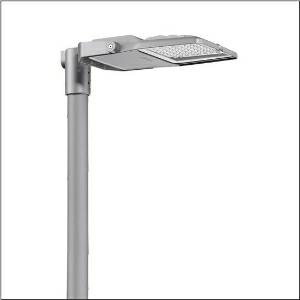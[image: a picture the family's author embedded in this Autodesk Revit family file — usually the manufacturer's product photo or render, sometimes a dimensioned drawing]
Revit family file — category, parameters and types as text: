
# Revit family: floodlight_fl_21_mini___pl61_5xa7771c4c3a_eca3
name_source: partatom
category: Lighting Fixtures
units: mm (PartAtom-declared; Revit-internal decimal feet)

## family parameters
Cut with Voids When Loaded = No
Host = Face
Light Source = No
Part Type = Normal
Room Calculation Point = No
Round Connector Dimension = Use Diameter
Shared = No

## types (1)
- --- (1 x LED, 12490 lm, 87.2 W, 4000K)
    Apparent Load = 87 VA
    CIE Flux Codes = 33 65 98 100 100
    Color Rendering = 70
    Color Temperature = 4000K
    Default Elevation = 1800 mm
    Description = Floodlight FL 21 mini, floodlight, primary light control with lens, of PMMA, primary optical cover: protective disc, of toughened safety glass, transparent, light distribution: PL61, light emission: direct distribution, installation type: surface-mounted, LED, High Power LED, rated luminous flux: 12.490lm, luminous efficacy: 143lm/W, light colour: 740, colour temperature: 4000K, control gear: ECG iQ, control: Auto-Match, Temp-Guard, Lumen-Switch, Night-Set, Smart-Wire, Light-Fading, Desk-Remote (wireless, voltage-free reading and setting of iQ features in the workshop via application-optimized NFC function/RFID function), optimised constant luminous flux control (CLO 2.0), with terminal, 6-pole, mains connection: 220..240V, AC, 50/60Hz, start of lifetime: 87W, end of lifetime: 92W, reduction: 40W, luminaire housing, of diecast aluminium, powder-coated, Siteco® metallic grey (DB 702S), corrosivity category C5 according to DIN EN ISO 12944, mast bracket, of steel, galvanised, powder-coated, Siteco® metallic grey (DB 702S), protection rating (complete): IP66, insulation class (complete): insulation class II (safety insulation), certification: CE, ENEC, VDE, protection symbol: D, impact resistance: IK08, permissible operating ambient temperature: -40..+40°C, permissible operating ambient temperature for outdoor applications: -40..+50°C, standard: DIN EN 12944, packaging unit: 1 piece

Light Distribution: PL61
    Height = 70 mm
    Lamp = 1 x LED
    Lamp Light Flux = 12490 lm
    Lamp Power = 87.2 W
    Lamp count = 1
    Length = 485 mm
    Luminous efficacy = 143 lm/W
    Manufacturer = Siteco
    ModVariant = No
    Model = 5XA7771C4C3A
    Number of Poles = 1
    OnlyDefault = Yes
    Power Factor = 1
    Product Name = Floodlight FL 21 mini | PL61
    Product group = floodlight | pylon top
    ProductGroupID = 6101
    Protection Class = Protection class II
    Protection Degree = IP 66
    RLX_Detail_Level = 1
    RlxData = <blob elided: 101169 chars, md5=6e81bd83>
    Socket = socket
    Standby Power = 0 W
    System Light Flux = 12490 lm
    System Power = 87 W
    Type Comments = factory setting: luminous flux: 100 % | dim-lin: 254 | 456 mA
    Type Image = l_1007125.jpg
    URL = http://relux.com
    VarID = @adj_085513
    Voltage = 0 V
    Weight = 0.00 kg
    Width = 337 mm

## geometry (parser evidence)
native form markers: Blend x4, Sweep x12
no freeform markers — native parametric forms only
